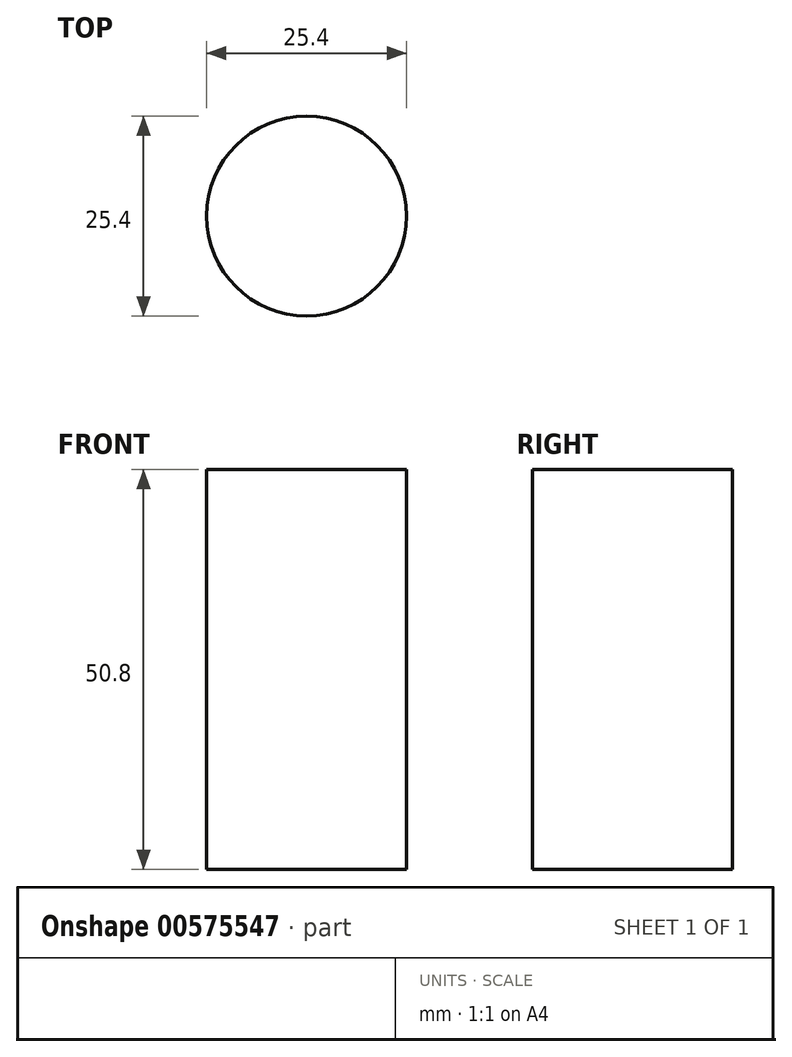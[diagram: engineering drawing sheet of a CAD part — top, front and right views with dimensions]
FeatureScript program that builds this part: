
annotation { "Feature Type Name" : "Feature", "Feature Type Description" : "" }
export const myFeature = defineFeature(function(context is Context, id is Id, definition is map)
    precondition{}
    {
        {
            var Q0;
            Q0=qCreatedBy(makeId("Top.planeOp"),FACE);
            var sketch = newSketch(context, id + "F0", { "sketchPlane" : qUnion([Q0])});
            skCircle(sketch, "E0", {"center": v(0, 0) * mm, "radius": 12.7 * mm});
            skSolve(sketch);
        }
        {
            var Q0;
            Q0=makeQuery(id+"F0.imprint","IMPRINT",FACE,{"disambiguationData":[TD([[makeQuery(id+"F0.imprint","IMPRINT",EDGE,{"derivedFrom":sQuery(id+"F0.wireOp",EDGE,"E0")}),1.0]])]});
            extrude(context, id + "F1", {"entities" : qUnion([Q0]), "endBound" : BoundingType.SYMMETRIC, "depth" : 50.8 * mm, "offsetDistance" : 25.4 * mm});
        }
    });
